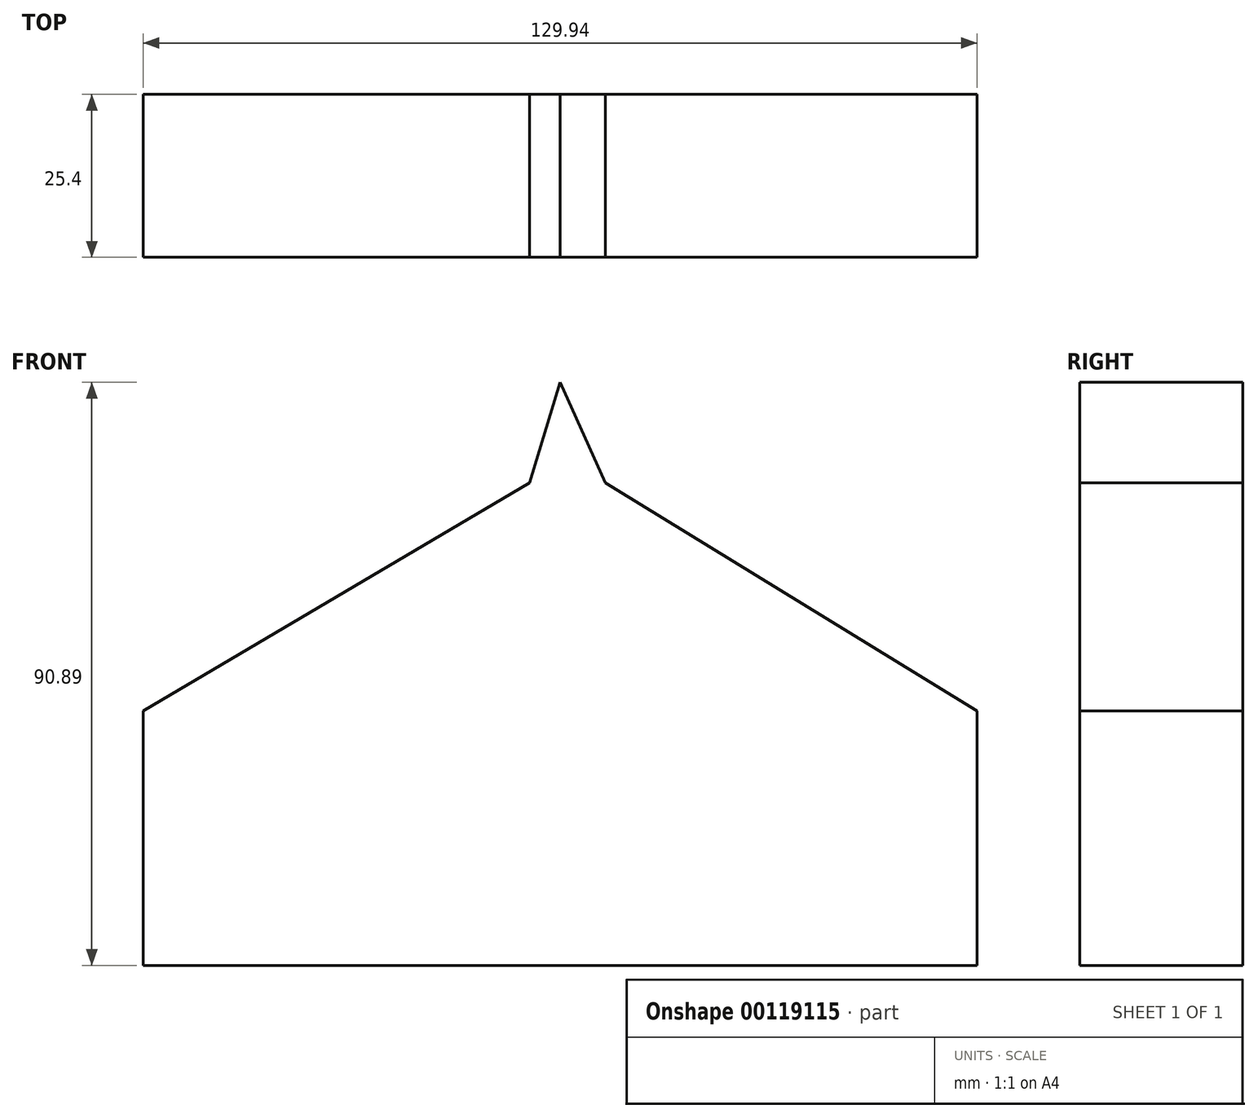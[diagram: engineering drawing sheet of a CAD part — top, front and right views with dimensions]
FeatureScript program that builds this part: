
annotation { "Feature Type Name" : "Feature", "Feature Type Description" : "" }
export const myFeature = defineFeature(function(context is Context, id is Id, definition is map)
    precondition{}
    {
        {
            var Q0;
            Q0=qCreatedBy(makeId("Front.planeOp"),FACE);
            var sketch = newSketch(context, id + "F0", { "sketchPlane" : qUnion([Q0])});
            skLineSegment(sketch, "E0.bottom", {"start": v(-64.97, -19.84) * mm, "end": v(64.97, -19.84) * mm});
            skLineSegment(sketch, "E0.top", {"start": v(-64.97, 19.84) * mm, "end": v(64.97, 19.84) * mm});
            skLineSegment(sketch, "E0.left", {"start": v(-64.97, -19.84) * mm, "end": v(-64.97, 19.84) * mm});
            skLineSegment(sketch, "E0.right", {"start": v(64.97, -19.84) * mm, "end": v(64.97, 19.84) * mm});
            skPoint(sketch, "E0.middle", {"position": v(0, 0) * mm});
            skLineSegment(sketch, "E1", {"start": v(-64.97, 19.84) * mm, "end": v(-4.8, 55.37) * mm});
            skLineSegment(sketch, "E2", {"start": v(-4.8, 55.37) * mm, "end": v(7.04, 55.37) * mm});
            skLineSegment(sketch, "E3", {"start": v(7.04, 55.37) * mm, "end": v(64.97, 19.84) * mm});
            skLineSegment(sketch, "E4", {"start": v(-4.8, 55.37) * mm, "end": v(0, 71.05) * mm});
            skLineSegment(sketch, "E5", {"start": v(0, 71.05) * mm, "end": v(7.04, 55.37) * mm});
            skSolve(sketch);
        }
        {
            var Q0;
            Q0 = qSketchRegion(id + "F0", true);
            extrude(context, id + "F1", {"entities" : qUnion([Q0]), "depth" : 25.4 * mm});
        }
    });
